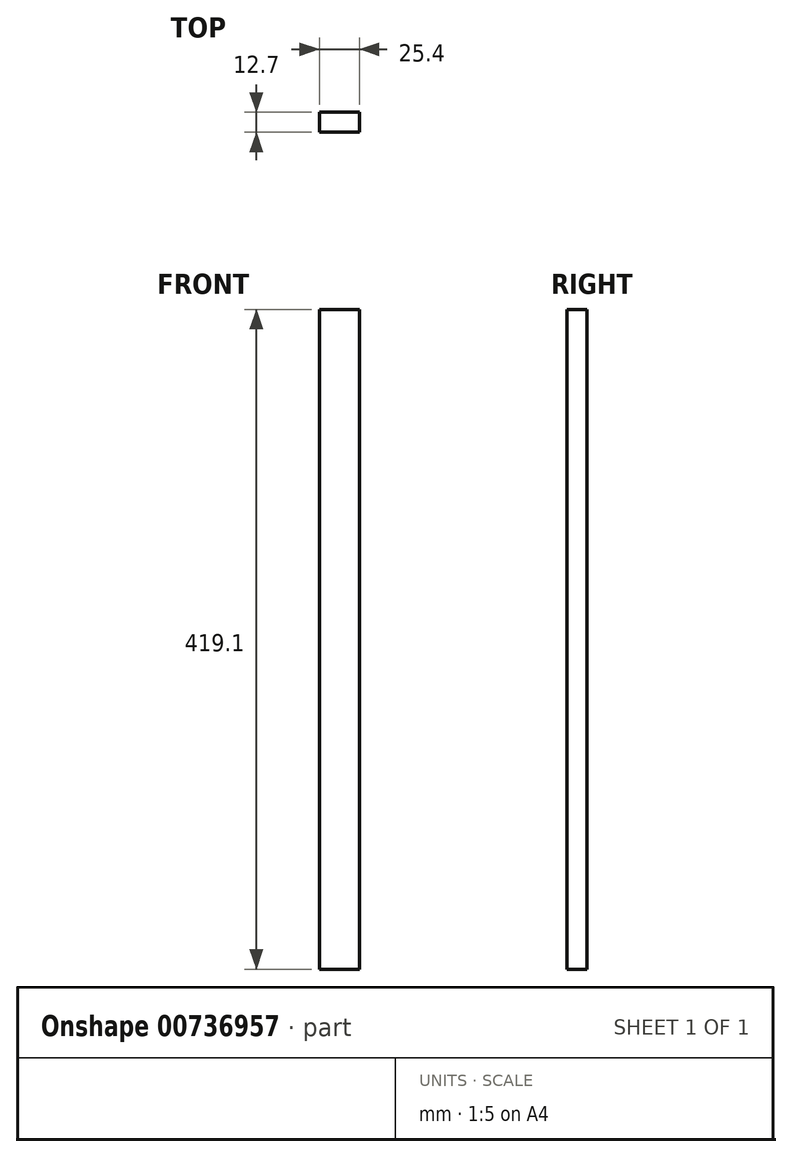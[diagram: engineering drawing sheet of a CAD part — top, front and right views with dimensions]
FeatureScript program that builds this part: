
annotation { "Feature Type Name" : "Feature", "Feature Type Description" : "" }
export const myFeature = defineFeature(function(context is Context, id is Id, definition is map)
    precondition{}
    {
        {
            var Q0;
            Q0=qCreatedBy(makeId("Front.planeOp"),FACE);
            var sketch = newSketch(context, id + "F0", { "sketchPlane" : qUnion([Q0])});
            skLineSegment(sketch, "E0.bottom", {"start": v(12.7, -209.55) * mm, "end": v(-12.7, -209.55) * mm});
            skLineSegment(sketch, "E0.top", {"start": v(12.7, 209.55) * mm, "end": v(-12.7, 209.55) * mm});
            skLineSegment(sketch, "E0.left", {"start": v(12.7, -209.55) * mm, "end": v(12.7, 209.55) * mm});
            skLineSegment(sketch, "E0.right", {"start": v(-12.7, -209.55) * mm, "end": v(-12.7, 209.55) * mm});
            skPoint(sketch, "E0.middle", {"position": v(0, 0) * mm});
            skSolve(sketch);
        }
        {
            var Q0;
            Q0=qSketchRegion(id+"F0",true);
            extrude(context, id + "F1", {"entities" : qUnion([Q0]), "depth" : 12.7 * mm, "offsetDistance" : 25.4 * mm});
        }
    });
